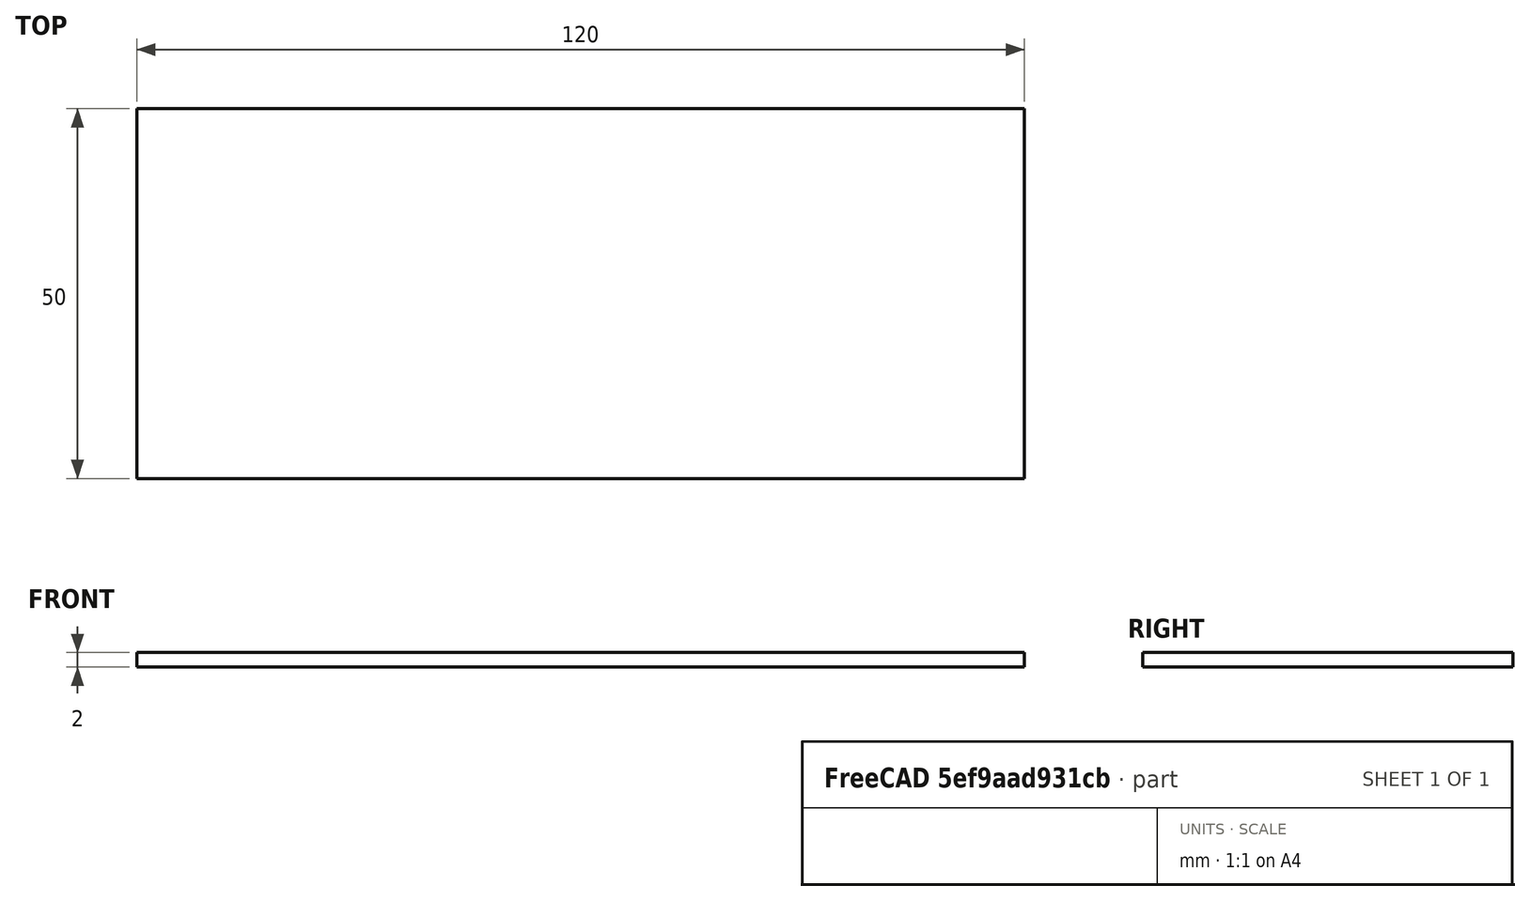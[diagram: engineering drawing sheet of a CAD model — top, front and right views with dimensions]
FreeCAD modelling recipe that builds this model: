
FCSTD DOCUMENT  (FreeCAD 1.0R39319 (Git))
Label: case
License: All rights reserved
LicenseURL: https://en.wikipedia.org/wiki/All_rights_reserved
objects: Sketcher::SketchObject×2, PartDesign::Pad×1, PartDesign::Body×1
note: 8 computed .brp shape members not serialized (recipe doc carries the construction recipe); baked Part::Feature solids carry a one-line shape summary decoded from their .brp

FEATURE [Sketcher::SketchObject] Sketch
  ArcFitTolerance = 1e-06
  AttachmentSupport = -> [XY_Plane]
  FullyConstrained = true
  MakeInternals = false
  MapMode = 5
  sketch-geometry (4):
    g0: LineSegment StartX=0 StartY=0 StartZ=0 EndX=120 EndY=0 EndZ=0
    g1: LineSegment StartX=120 StartY=0 StartZ=0 EndX=120 EndY=50 EndZ=0
    g2: LineSegment StartX=120 StartY=50 StartZ=0 EndX=0 EndY=50 EndZ=0
    g3: LineSegment StartX=0 StartY=50 StartZ=0 EndX=0 EndY=0 EndZ=0
  constraints (11):
    c: Coincident(g0,g1)
    c: Coincident(g1,g2)
    c: Coincident(g2,g3)
    c: Coincident(g3,g0)
    c: Horizontal(g0)
    c: Horizontal(g2)
    c: Vertical(g1)
    c: Vertical(g3)
    c: Distance(g1,g3) = 120
    c: Distance(g0,g2) = 50
    c: Coincident(g0,g-1)
FEATURE [PartDesign::Pad] Pad
  Direction = (0,0,1)
  Length = 2
  Length2 = 10
  Profile = -> Sketch
  ReferenceAxis = -> Sketch [N_Axis]
  Refine = true
  Suppressed = false
  Type = 0
FEATURE [Sketcher::SketchObject] Sketch001
  ArcFitTolerance = 1e-06
  AttachmentSupport = -> [Pad]
  ExternalGeometry = -> [Pad]
  FullyConstrained = false
  MakeInternals = false
  MapMode = 5
  Placement = pos=(0,0,2) rot=(0,0,1;0rad)
  sketch-geometry (1):
    g0: Circle CenterX=2.50508 CenterY=50 CenterZ=0 NormalX=0 NormalY=0 NormalZ=1 AngleXU=0 Radius=0.75
  constraints (2):
    c: Diameter(g0) = 1.5
    c: Horizontal(g0,g-4)
FEATURE [PartDesign::Body] Body
  AllowCompound = false
  Group = -> [Sketch,Pad,Sketch001]
  Origin = -> Origin
  Tip = -> Pad
